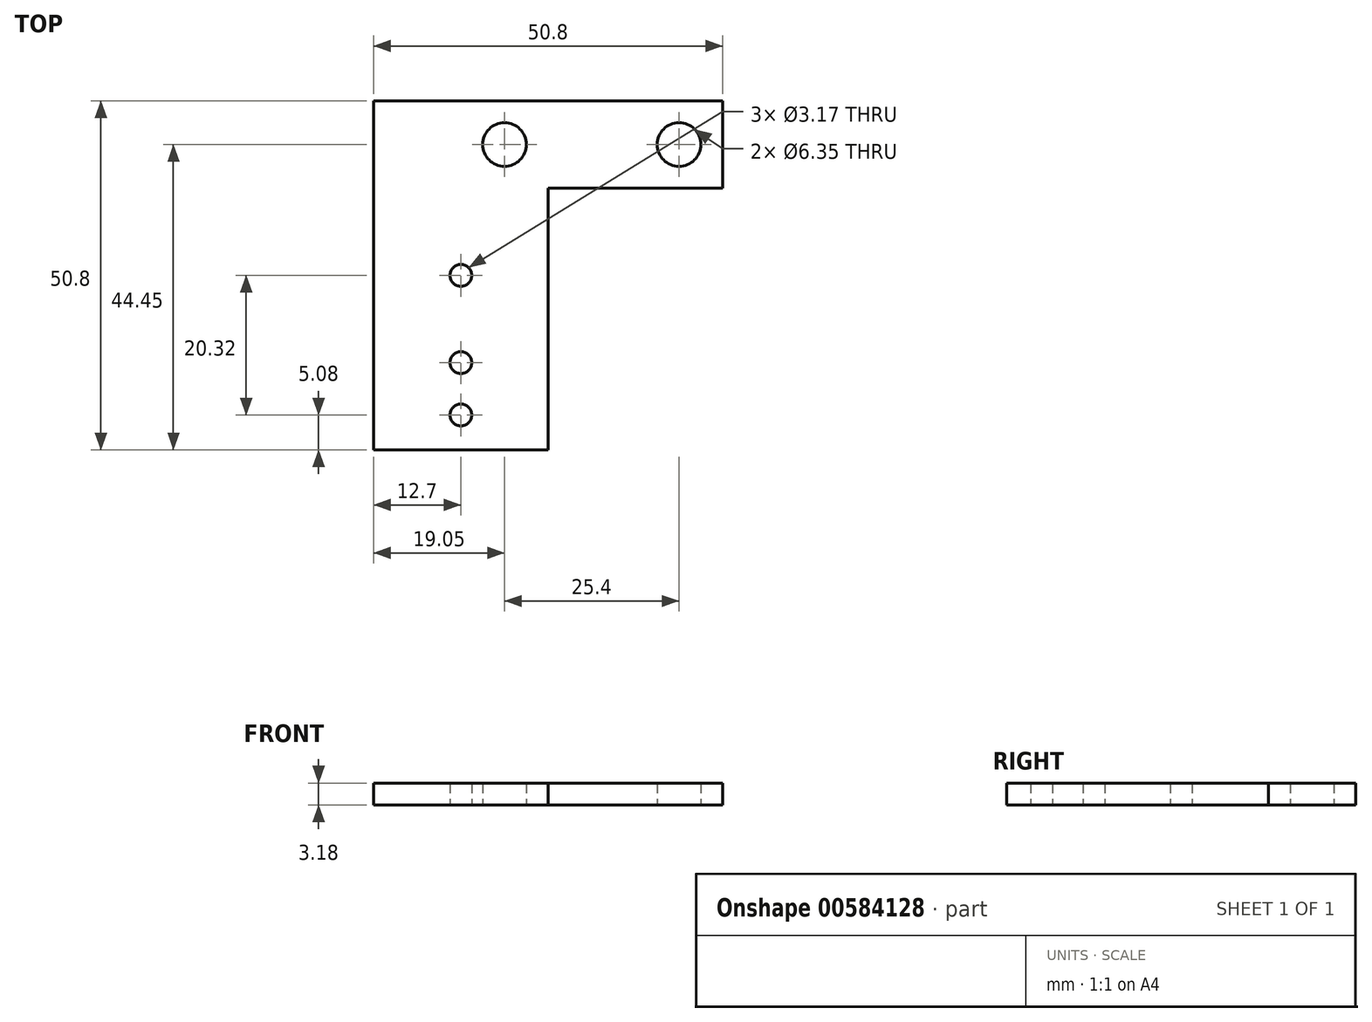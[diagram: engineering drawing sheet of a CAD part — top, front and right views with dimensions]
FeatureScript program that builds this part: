
annotation { "Feature Type Name" : "Feature", "Feature Type Description" : "" }
export const myFeature = defineFeature(function(context is Context, id is Id, definition is map)
    precondition{}
    {
        {
            var Q0;
            Q0=qCreatedBy(makeId("Top.planeOp"),FACE);
            var sketch = newSketch(context, id + "F0", { "sketchPlane" : qUnion([Q0])});
            skLineSegment(sketch, "E0.bottom", {"start": v(-50.8, 38.1) * mm, "end": v(-25.4, 38.1) * mm});
            skLineSegment(sketch, "E0.top", {"start": v(-50.8, 0) * mm, "end": v(-25.4, 0) * mm});
            skLineSegment(sketch, "E0.left", {"start": v(-50.8, 38.1) * mm, "end": v(-50.8, 0) * mm});
            skLineSegment(sketch, "E0.right", {"start": v(-25.4, 38.1) * mm, "end": v(-25.4, 0) * mm});
            skLineSegment(sketch, "E1.bottom", {"start": v(-50.8, 38.1) * mm, "end": v(0, 38.1) * mm});
            skLineSegment(sketch, "E1.top", {"start": v(-50.8, 50.8) * mm, "end": v(0, 50.8) * mm});
            skLineSegment(sketch, "E1.left", {"start": v(-50.8, 38.1) * mm, "end": v(-50.8, 50.8) * mm});
            skLineSegment(sketch, "E1.right", {"start": v(0, 38.1) * mm, "end": v(0, 50.8) * mm});
            skCircle(sketch, "E2", {"center": v(-6.35, 44.45) * mm, "radius": 3.18 * mm});
            skCircle(sketch, "E3", {"center": v(-31.75, 44.45) * mm, "radius": 3.18 * mm});
            skCircle(sketch, "E4", {"center": v(-38.1, 25.4) * mm, "radius": 1.59 * mm});
            skCircle(sketch, "E5", {"center": v(-38.1, 12.7) * mm, "radius": 1.59 * mm});
            skCircle(sketch, "E6", {"center": v(-38.1, 5.08) * mm, "radius": 1.59 * mm});
            skSolve(sketch);
        }
        {
            var Q0;
            Q0 = qSketchRegion(id + "F0", true);
            extrude(context, id + "F1", {"entities" : qUnion([Q0]), "depth" : 3.17 * mm, "offsetDistance" : 25.4 * mm});
        }
    });
